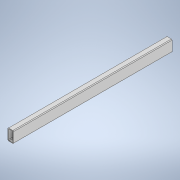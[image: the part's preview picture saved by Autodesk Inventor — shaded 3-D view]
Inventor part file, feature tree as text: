
AUTODESK INVENTOR PART (.ipt)
format: ipt  version: 2020 (Build 240168000, 168)  size: 126,464 bytes
history: native  units: in
note: dims shown in document units (in); Inventor stores cm internally (conversion verified against a paired STEP export)
features: extrude x1, sketch x1
ambient origin geometry x8: Origin, YZ Plane, XZ Plane, XY Plane, X Axis, Y Axis, Z Axis, Center Point
bodies: Solid1 (feature_tree)
feature tree (2):
  extrude  "Extrusion1"  Depth=1.0in
  sketch  "Sketch1"  dims[d0=2.0in d1=1.0in d2=0.125in d3=0.125in d4=0.125in d5=0.125in d6=0.125in d7=0.125in d8=0.125in d9=0.125in d10=0.125in d11=28.0in d12=0.0in]
